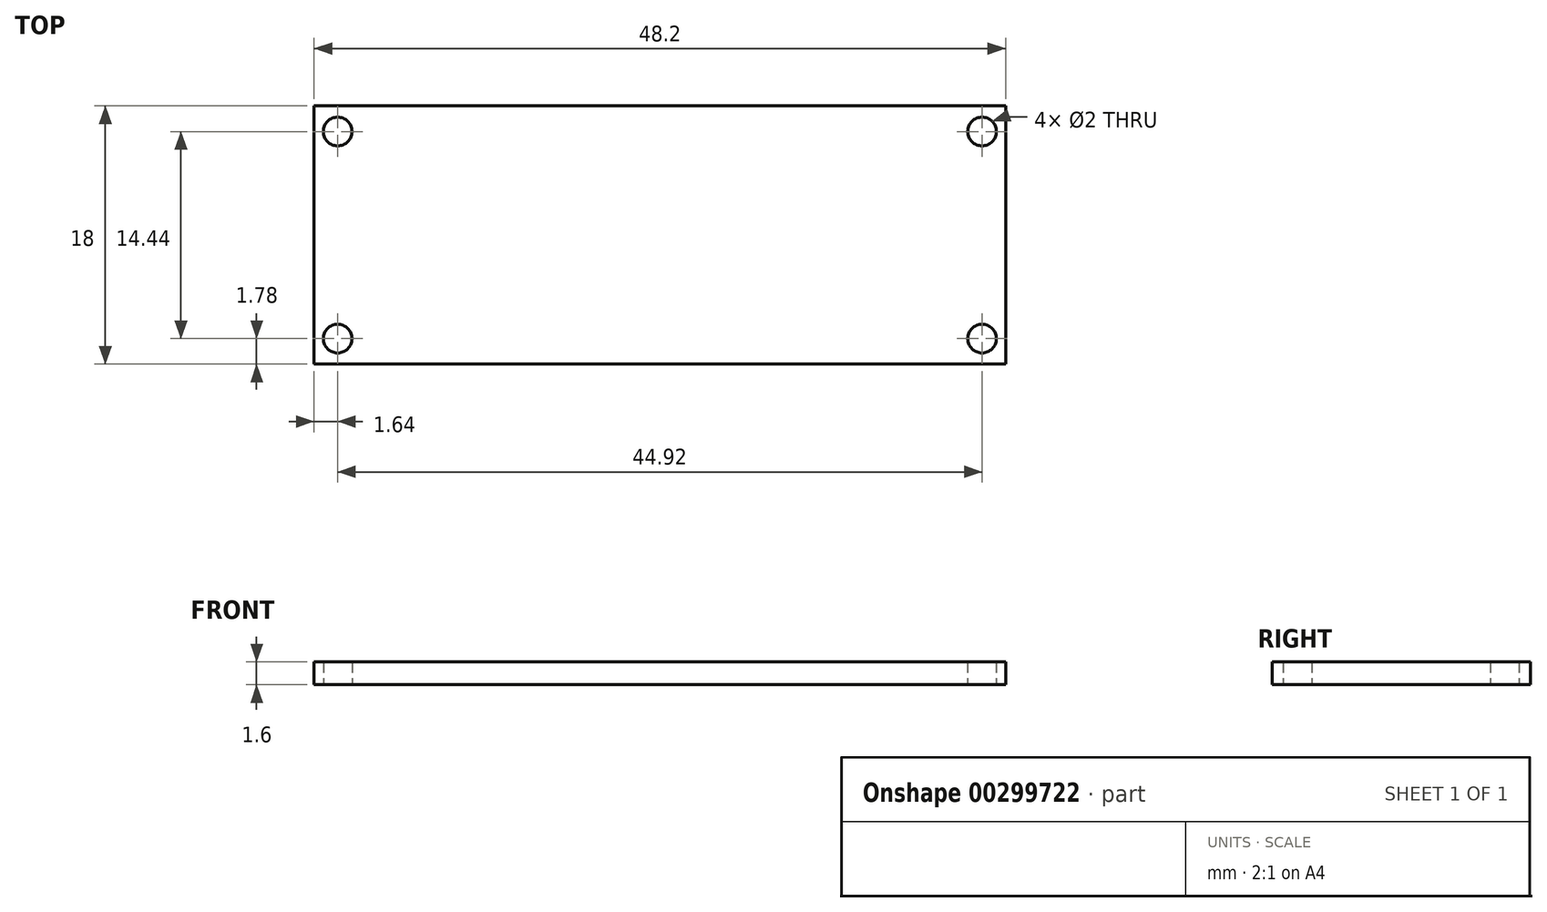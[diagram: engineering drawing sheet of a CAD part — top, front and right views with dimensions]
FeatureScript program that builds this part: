
annotation { "Feature Type Name" : "Feature", "Feature Type Description" : "" }
export const myFeature = defineFeature(function(context is Context, id is Id, definition is map)
    precondition{}
    {
        {
            var Q0;
            Q0=qCreatedBy(makeId("Top.planeOp"),FACE);
            var sketch = newSketch(context, id + "F0", { "sketchPlane" : qUnion([Q0])});
            skLineSegment(sketch, "E0.bottom", {"start": v(24.1, 9) * mm, "end": v(-24.1, 9) * mm});
            skLineSegment(sketch, "E0.top", {"start": v(24.1, -9) * mm, "end": v(-24.1, -9) * mm});
            skLineSegment(sketch, "E0.left", {"start": v(24.1, 9) * mm, "end": v(24.1, -9) * mm});
            skLineSegment(sketch, "E0.right", {"start": v(-24.1, 9) * mm, "end": v(-24.1, -9) * mm});
            skPoint(sketch, "E0.middle", {"position": v(0, 0) * mm});
            skCircle(sketch, "E1", {"center": v(-22.46, 7.22) * mm, "radius": 1 * mm});
            skLineSegment(sketch, "E2", {"start": v(0, 0) * mm, "end": v(0, 9) * mm, "construction": true});
            skLineSegment(sketch, "E3", {"start": v(0, 0) * mm, "end": v(24.1, 0) * mm, "construction": true});
            skCircle(sketch, "E4.MirrorC", {"center": v(22.46, 7.22) * mm, "radius": 1 * mm});
            skCircle(sketch, "E5.MirrorC", {"center": v(-22.46, -7.22) * mm, "radius": 1 * mm});
            skCircle(sketch, "E6.MirrorC", {"center": v(22.46, -7.22) * mm, "radius": 1 * mm});
            skSolve(sketch);
        }
        {
            var Q0;
            Q0=makeQuery(id+"F0.imprint","IMPRINT",FACE,{"disambiguationData":[TD([[makeQuery(id+"F0.imprint","IMPRINT",EDGE,{"derivedFrom":sQuery(id+"F0.wireOp",EDGE,"E0.bottom")}),1.0]])]});
            extrude(context, id + "F1", {"entities" : qUnion([Q0]), "depth" : 1.6 * mm});
        }
    });
